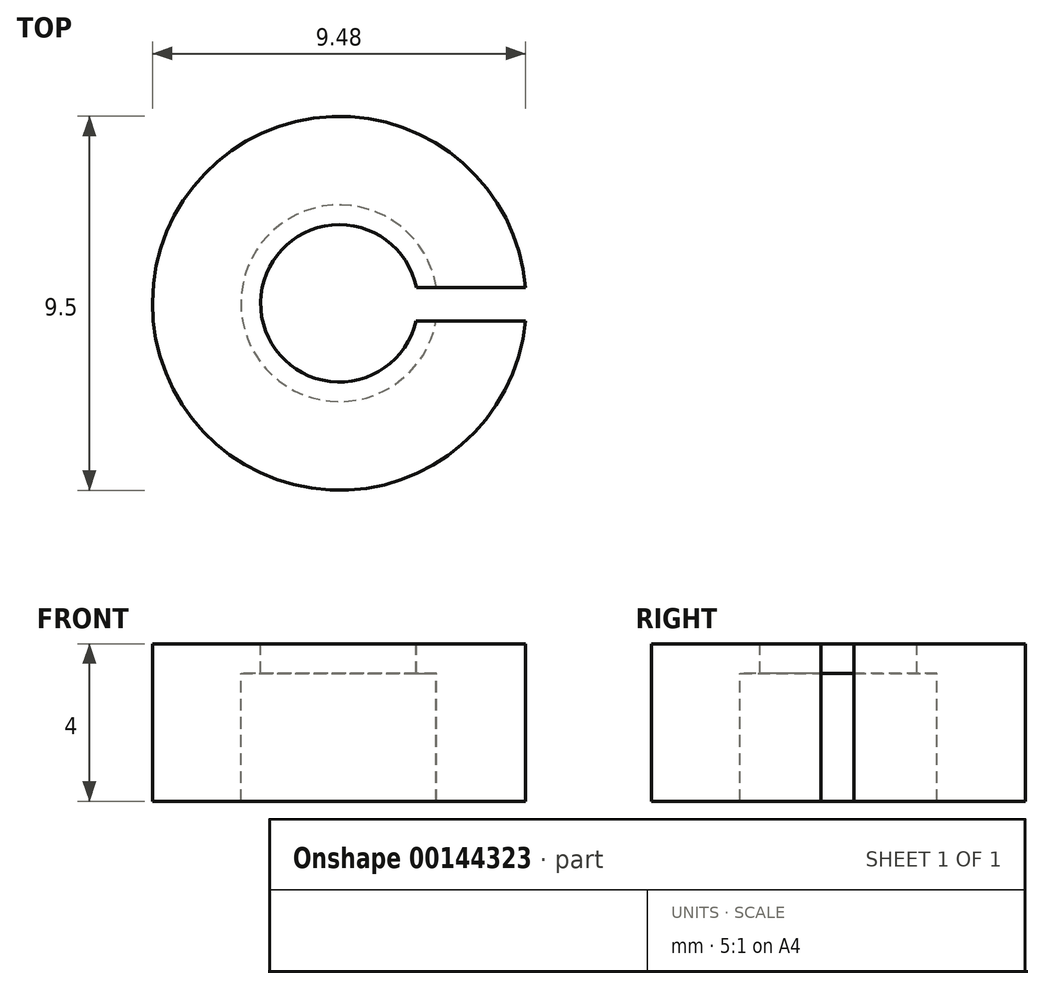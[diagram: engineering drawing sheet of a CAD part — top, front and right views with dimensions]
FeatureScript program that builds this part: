
annotation { "Feature Type Name" : "Feature", "Feature Type Description" : "" }
export const myFeature = defineFeature(function(context is Context, id is Id, definition is map)
    precondition{}
    {
        {
            var Q0;
            Q0=qCreatedBy(makeId("Top.planeOp"),FACE);
            var sketch = newSketch(context, id + "F0", { "sketchPlane" : qUnion([Q0])});
            skCircle(sketch, "E0", {"center": v(0, 0) * mm, "radius": 4.75 * mm});
            skSolve(sketch);
        }
        {
            var Q0;
            Q0 = qSketchRegion(id + "F0", true);
            extrude(context, id + "F1", {"entities" : qUnion([Q0]), "depth" : 4 * mm});
        }
        {
            var Q0;
            Q0=makeQuery(id+"F1.opExtrude","CAP_FACE",FACE,{"disambiguationData":[OSD([sQuery(id+"F0.wireOp",EDGE,"E0")])],"isStart":false});
            var sketch = newSketch(context, id + "F2", { "sketchPlane" : qUnion([Q0])});
            skCircle(sketch, "E1", {"center": v(0, 0) * mm, "radius": 2 * mm});
            skSolve(sketch);
        }
        {
            var Q0;
            Q0 = qSketchRegion(id + "F2", true);
            extrude(context, id + "F3", {"entities" : qUnion([Q0]), "operationType" : NewBodyOperationType.REMOVE, "oppositeDirection" : true, "depth" : 4 * mm});
        }
        {
            var Q0;
            Q0=makeQuery(id+"F1.opExtrude","CAP_FACE",FACE,{"disambiguationData":[OSD([sQuery(id+"F0.wireOp",EDGE,"E0")])],"isStart":false});
            var sketch = newSketch(context, id + "F4", { "sketchPlane" : qUnion([Q0])});
            skCircle(sketch, "E2", {"center": v(0, 0) * mm, "radius": 2.5 * mm});
            skSolve(sketch);
        }
        {
            var Q0;
            Q0 = qSketchRegion(id + "F4", true);
            extrude(context, id + "F5", {"entities" : qUnion([Q0]), "operationType" : NewBodyOperationType.REMOVE, "oppositeDirection" : true, "depth" : 4 * mm, "hasSecondDirection" : true, "secondDirectionOppositeDirection" : true, "secondDirectionDepth" : 0.75 * mm});
        }
        {
            var Q0;
            Q0=makeQuery(id+"F1.opExtrude","CAP_FACE",FACE,{"disambiguationData":[OSD([sQuery(id+"F0.wireOp",EDGE,"E0")])],"isStart":false});
            var sketch = newSketch(context, id + "F6", { "sketchPlane" : qUnion([Q0])});
            skLineSegment(sketch, "E3.bottom", {"start": v(1.41, 0.4) * mm, "end": v(5.2, 0.4) * mm});
            skLineSegment(sketch, "E3.top", {"start": v(1.41, -0.45) * mm, "end": v(5.2, -0.45) * mm});
            skLineSegment(sketch, "E3.left", {"start": v(1.41, 0.4) * mm, "end": v(1.41, -0.45) * mm});
            skLineSegment(sketch, "E3.right", {"start": v(5.2, 0.4) * mm, "end": v(5.2, -0.45) * mm});
            skSolve(sketch);
        }
        {
            var Q0;
            Q0 = qSketchRegion(id + "F6", true);
            extrude(context, id + "F7", {"entities" : qUnion([Q0]), "operationType" : NewBodyOperationType.REMOVE, "oppositeDirection" : true, "depth" : 4 * mm});
        }
    });
